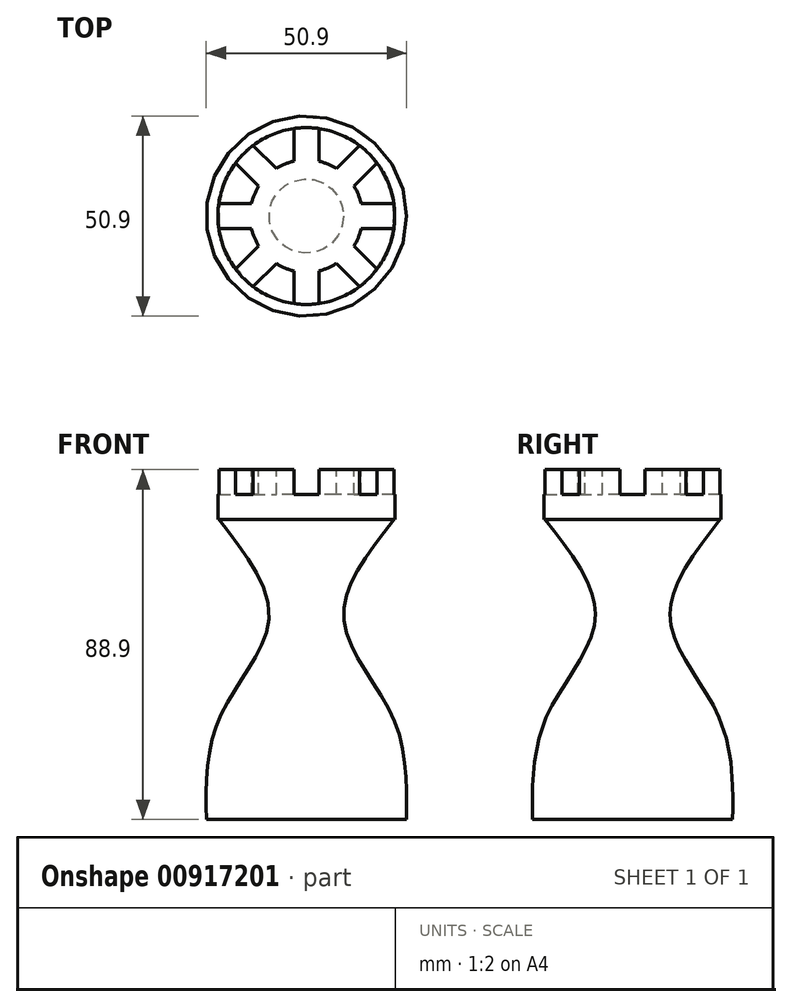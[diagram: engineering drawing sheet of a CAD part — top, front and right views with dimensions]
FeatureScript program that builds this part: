
annotation { "Feature Type Name" : "Feature", "Feature Type Description" : "" }
export const myFeature = defineFeature(function(context is Context, id is Id, definition is map)
    precondition{}
    {
        {
            var Q0;
            Q0=qCreatedBy(makeId("Top.planeOp"),FACE);
            var sketch = newSketch(context, id + "F0", { "sketchPlane" : qUnion([Q0])});
            skCircle(sketch, "E0", {"center": v(0, 0) * mm, "radius": 25.4 * mm});
            skSolve(sketch);
        }
        {
            var Q0;
            Q0=qCreatedBy(makeId("Top.planeOp"),FACE);
            cPlane(context, id + "F1", {"entities" : qUnion([Q0]), "cplaneType" : CPlaneType.OFFSET, "offset" : 25.4 * mm, "width" : 152.4 * mm, "height" : 152.4 * mm});
        }
        {
            var Q0;
            Q0=qCreatedBy(id+"F1.planeOp",FACE);
            var sketch = newSketch(context, id + "F2", { "sketchPlane" : qUnion([Q0])});
            skCircle(sketch, "E1", {"center": v(0, 0) * mm, "radius": 22.23 * mm});
            skSolve(sketch);
        }
        {
            var Q0;
            Q0=qCreatedBy(id+"F1.planeOp",FACE);
            cPlane(context, id + "F3", {"entities" : qUnion([Q0]), "cplaneType" : CPlaneType.OFFSET, "offset" : 25.4 * mm, "width" : 152.4 * mm, "height" : 152.4 * mm});
        }
        {
            var Q0;
            Q0=qCreatedBy(id+"F3.planeOp",FACE);
            var sketch = newSketch(context, id + "F4", { "sketchPlane" : qUnion([Q0])});
            skCircle(sketch, "E2", {"center": v(0, 0) * mm, "radius": 9.52 * mm});
            skSolve(sketch);
        }
        {
            var Q0;
            Q0=qCreatedBy(id+"F3.planeOp",FACE);
            cPlane(context, id + "F5", {"entities" : qUnion([Q0]), "cplaneType" : CPlaneType.OFFSET, "offset" : 25.4 * mm, "width" : 152.4 * mm, "height" : 152.4 * mm});
        }
        {
            var Q0;
            Q0=qCreatedBy(id+"F5.planeOp",FACE);
            var sketch = newSketch(context, id + "F6", { "sketchPlane" : qUnion([Q0])});
            skCircle(sketch, "E3", {"center": v(0, 0) * mm, "radius": 22.23 * mm});
            skSolve(sketch);
        }
        {
            var Q0;
            Q0 = qSketchRegion(id + "F0", true);
            var Q1;
            Q1 = qSketchRegion(id + "F2", true);
            var Q2;
            Q2 = qSketchRegion(id + "F4", true);
            var Q3;
            Q3 = qSketchRegion(id + "F6", true);
            loft(context, id + "F7", {"sheetProfilesArray" : [{ "sheetProfileEntities" : qUnion([Q0]) }, { "sheetProfileEntities" : qUnion([Q1]) }, { "sheetProfileEntities" : qUnion([Q2]) }, { "sheetProfileEntities" : qUnion([Q3]) }]});
        }
        {
            var Q0;
            Q0=makeQuery(id+"F7.opLoft","CAP_FACE",FACE,{"disambiguationData":[OSD([makeQuery(id+"F6.imprint","IMPRINT",FACE,{"disambiguationData":[TD([[makeQuery(id+"F6.imprint","IMPRINT",EDGE,{"derivedFrom":sQuery(id+"F6.wireOp",EDGE,"E3")}),1.0]])]})])],"isStart":true});
            var sketch = newSketch(context, id + "F8", { "sketchPlane" : qUnion([Q0])});
            skCircle(sketch, "E4", {"center": v(0, 0) * mm, "radius": 22.46 * mm});
            skFitSpline(sketch, "E5.0", {"points": [v(22.23, 0) * mm, v(22.23, 0.7) * mm, v(22.2, 1.42) * mm, v(22.12, 2.14) * mm, v(22.12, 2.18) * mm, v(22.05, 2.86) * mm, v(21.95, 3.58) * mm, v(21.8, 4.3) * mm, v(21.8, 4.34) * mm, v(21.66, 5.01) * mm, v(21.49, 5.72) * mm, v(21.28, 6.41) * mm, v(21.27, 6.45) * mm, v(21.07, 7.11) * mm, v(20.82, 7.8) * mm, v(20.55, 8.47) * mm, v(20.53, 8.5) * mm, v(20.27, 9.14) * mm, v(19.96, 9.8) * mm, v(19.62, 10.44) * mm, v(19.6, 10.48) * mm, v(19.28, 11.08) * mm, v(18.9, 11.7) * mm, v(18.5, 12.32) * mm, v(18.48, 12.35) * mm, v(18.1, 12.92) * mm, v(17.66, 13.5) * mm, v(17.2, 14.07) * mm, v(17.18, 14.1) * mm, v(16.74, 14.63) * mm, v(16.26, 15.17) * mm, v(15.74, 15.69) * mm, v(15.72, 15.72) * mm, v(15.23, 16.2) * mm, v(14.7, 16.7) * mm, v(14.13, 17.16) * mm, v(14.1, 17.18) * mm, v(13.57, 17.62) * mm, v(12.98, 18.05) * mm, v(12.38, 18.46) * mm, v(12.35, 18.48) * mm, v(11.77, 18.86) * mm, v(11.15, 19.24) * mm, v(10.51, 19.58) * mm, v(10.48, 19.6) * mm, v(9.87, 19.93) * mm, v(9.21, 20.24) * mm, v(8.54, 20.52) * mm, v(8.5, 20.53) * mm, v(7.87, 20.8) * mm, v(7.18, 21.04) * mm, v(6.49, 21.26) * mm, v(6.45, 21.27) * mm, v(5.8, 21.47) * mm, v(5.09, 21.65) * mm, v(4.37, 21.8) * mm, v(4.34, 21.8) * mm, v(3.66, 21.93) * mm, v(2.94, 22.04) * mm, v(2.22, 22.11) * mm, v(2.18, 22.12) * mm, v(1.5, 22.19) * mm, v(0.77, 22.22) * mm, v(0.04, 22.22) * mm, v(0, 22.23) * mm, v(-0.69, 22.23) * mm, v(-1.42, 22.2) * mm, v(-2.14, 22.12) * mm, v(-2.18, 22.12) * mm, v(-2.86, 22.05) * mm, v(-3.58, 21.95) * mm, v(-4.3, 21.8) * mm, v(-4.34, 21.8) * mm, v(-5.01, 21.66) * mm, v(-5.72, 21.49) * mm, v(-6.41, 21.28) * mm, v(-6.45, 21.27) * mm, v(-7.11, 21.07) * mm, v(-7.8, 20.82) * mm, v(-8.47, 20.55) * mm, v(-8.5, 20.53) * mm, v(-9.14, 20.27) * mm, v(-9.8, 19.96) * mm, v(-10.44, 19.62) * mm, v(-10.48, 19.6) * mm, v(-11.08, 19.28) * mm, v(-11.7, 18.9) * mm, v(-12.32, 18.5) * mm, v(-12.35, 18.48) * mm, v(-12.92, 18.1) * mm, v(-13.5, 17.66) * mm, v(-14.07, 17.2) * mm, v(-14.1, 17.18) * mm, v(-14.63, 16.74) * mm, v(-15.17, 16.26) * mm, v(-15.69, 15.74) * mm, v(-15.72, 15.72) * mm, v(-16.2, 15.23) * mm, v(-16.7, 14.7) * mm, v(-17.16, 14.13) * mm, v(-17.18, 14.1) * mm, v(-17.62, 13.57) * mm, v(-18.05, 12.98) * mm, v(-18.46, 12.38) * mm, v(-18.48, 12.35) * mm, v(-18.86, 11.77) * mm, v(-19.24, 11.15) * mm, v(-19.58, 10.51) * mm, v(-19.6, 10.48) * mm, v(-19.93, 9.87) * mm, v(-20.24, 9.21) * mm, v(-20.52, 8.54) * mm, v(-20.53, 8.5) * mm, v(-20.8, 7.87) * mm, v(-21.04, 7.18) * mm, v(-21.26, 6.49) * mm, v(-21.27, 6.45) * mm, v(-21.47, 5.8) * mm, v(-21.65, 5.09) * mm, v(-21.8, 4.37) * mm, v(-21.8, 4.34) * mm, v(-21.93, 3.66) * mm, v(-22.04, 2.94) * mm, v(-22.11, 2.22) * mm, v(-22.12, 2.18) * mm, v(-22.19, 1.5) * mm, v(-22.22, 0.77) * mm, v(-22.22, 0.04) * mm, v(-22.23, 0) * mm, v(-22.23, -0.69) * mm, v(-22.2, -1.42) * mm, v(-22.12, -2.14) * mm, v(-22.12, -2.18) * mm, v(-22.05, -2.86) * mm, v(-21.95, -3.58) * mm, v(-21.8, -4.3) * mm, v(-21.8, -4.34) * mm, v(-21.66, -5.01) * mm, v(-21.49, -5.72) * mm, v(-21.28, -6.41) * mm, v(-21.27, -6.45) * mm, v(-21.07, -7.11) * mm, v(-20.82, -7.8) * mm, v(-20.55, -8.47) * mm, v(-20.53, -8.5) * mm, v(-20.27, -9.14) * mm, v(-19.96, -9.8) * mm, v(-19.62, -10.44) * mm, v(-19.6, -10.48) * mm, v(-19.28, -11.08) * mm, v(-18.9, -11.7) * mm, v(-18.5, -12.32) * mm, v(-18.48, -12.35) * mm, v(-18.1, -12.92) * mm, v(-17.66, -13.5) * mm, v(-17.2, -14.07) * mm, v(-17.18, -14.1) * mm, v(-16.74, -14.63) * mm, v(-16.26, -15.17) * mm, v(-15.74, -15.69) * mm, v(-15.72, -15.72) * mm, v(-15.23, -16.2) * mm, v(-14.7, -16.7) * mm, v(-14.13, -17.16) * mm, v(-14.1, -17.18) * mm, v(-13.57, -17.62) * mm, v(-12.98, -18.05) * mm, v(-12.38, -18.46) * mm, v(-12.35, -18.48) * mm, v(-11.77, -18.86) * mm, v(-11.15, -19.24) * mm, v(-10.51, -19.58) * mm, v(-10.48, -19.6) * mm, v(-9.87, -19.93) * mm, v(-9.21, -20.24) * mm, v(-8.54, -20.52) * mm, v(-8.5, -20.53) * mm, v(-7.87, -20.8) * mm, v(-7.18, -21.04) * mm, v(-6.49, -21.26) * mm, v(-6.45, -21.27) * mm, v(-5.8, -21.47) * mm, v(-5.09, -21.65) * mm, v(-4.37, -21.8) * mm, v(-4.34, -21.8) * mm, v(-3.66, -21.93) * mm, v(-2.94, -22.04) * mm, v(-2.22, -22.11) * mm, v(-2.18, -22.12) * mm, v(-1.5, -22.19) * mm, v(-0.77, -22.22) * mm, v(-0.04, -22.22) * mm, v(0, -22.23) * mm, v(0.69, -22.23) * mm, v(1.42, -22.2) * mm, v(2.14, -22.12) * mm, v(2.18, -22.12) * mm, v(2.86, -22.05) * mm, v(3.58, -21.95) * mm, v(4.3, -21.8) * mm, v(4.34, -21.8) * mm, v(5.01, -21.66) * mm, v(5.72, -21.49) * mm, v(6.41, -21.28) * mm, v(6.45, -21.27) * mm, v(7.11, -21.07) * mm, v(7.8, -20.82) * mm, v(8.47, -20.55) * mm, v(8.5, -20.53) * mm, v(9.14, -20.27) * mm, v(9.8, -19.96) * mm, v(10.44, -19.62) * mm, v(10.48, -19.6) * mm, v(11.08, -19.28) * mm, v(11.7, -18.9) * mm, v(12.32, -18.5) * mm, v(12.35, -18.48) * mm, v(12.92, -18.1) * mm, v(13.5, -17.66) * mm, v(14.07, -17.2) * mm, v(14.1, -17.18) * mm, v(14.63, -16.74) * mm, v(15.17, -16.26) * mm, v(15.69, -15.74) * mm, v(15.72, -15.72) * mm, v(16.2, -15.23) * mm, v(16.7, -14.7) * mm, v(17.16, -14.13) * mm, v(17.18, -14.1) * mm, v(17.62, -13.57) * mm, v(18.05, -12.98) * mm, v(18.46, -12.38) * mm, v(18.48, -12.35) * mm, v(18.86, -11.77) * mm, v(19.24, -11.15) * mm, v(19.58, -10.51) * mm, v(19.6, -10.48) * mm, v(19.93, -9.87) * mm, v(20.24, -9.21) * mm, v(20.52, -8.54) * mm, v(20.53, -8.5) * mm, v(20.8, -7.87) * mm, v(21.04, -7.18) * mm, v(21.26, -6.49) * mm, v(21.27, -6.45) * mm, v(21.47, -5.8) * mm, v(21.65, -5.09) * mm, v(21.8, -4.37) * mm, v(21.8, -4.34) * mm, v(21.93, -3.66) * mm, v(22.04, -2.94) * mm, v(22.11, -2.22) * mm, v(22.12, -2.18) * mm, v(22.19, -1.45) * mm, v(22.23, -0.73) * mm, v(22.23, 0) * mm, v(22.23, 0) * mm]});
            skSolve(sketch);
        }
        {
            var Q0;
            Q0 = qSketchRegion(id + "F8", true);
            var Q1;
            Q1=makeQuery(id+"F8.imprint","IMPRINT",FACE,{"disambiguationData":[TD([[makeQuery(id+"F8.imprint","IMPRINT",EDGE,{"derivedFrom":sQuery(id+"F8.wireOp",EDGE,"E5.0")}),1.0]])]});
            extrude(context, id + "F9", {"entities" : qUnion([Q0, Q1]), "depth" : 12.7 * mm, "offsetDistance" : 25.4 * mm});
        }
        {
            var Q0;
            Q0=makeQuery(id+"F9.opExtrude","CAP_FACE",FACE,{"disambiguationData":[OSD([sQuery(id+"F8.wireOp",EDGE,"E4")])],"isStart":false});
            var sketch = newSketch(context, id + "F10", { "sketchPlane" : qUnion([Q0])});
            skLineSegment(sketch, "E6", {"start": v(0, 0) * mm, "end": v(19.57, 0) * mm, "construction": true});
            skCircle(sketch, "E7", {"center": v(0, 0) * mm, "radius": 14.29 * mm});
            skLineSegment(sketch, "E8.bottom", {"start": v(27.54, -3.17) * mm, "end": v(11.6, -3.17) * mm});
            skLineSegment(sketch, "E8.top", {"start": v(27.54, 3.18) * mm, "end": v(11.6, 3.18) * mm});
            skLineSegment(sketch, "E8.left", {"start": v(27.54, -3.17) * mm, "end": v(27.54, 3.18) * mm});
            skLineSegment(sketch, "E8.right", {"start": v(11.6, -3.17) * mm, "end": v(11.6, 3.18) * mm});
            skPoint(sketch, "E8.middle", {"position": v(19.57, 0) * mm});
            skLineSegment(sketch, "E9.1.0", {"start": v(17.23, 21.72) * mm, "end": v(5.96, 10.45) * mm});
            skLineSegment(sketch, "E9.1.1", {"start": v(21.72, 17.23) * mm, "end": v(10.45, 5.96) * mm});
            skLineSegment(sketch, "E9.1.2", {"start": v(21.72, 17.23) * mm, "end": v(17.23, 21.72) * mm});
            skPoint(sketch, "E9.1.3", {"position": v(13.84, 13.84) * mm});
            skLineSegment(sketch, "E9.1.4", {"start": v(10.45, 5.96) * mm, "end": v(5.96, 10.45) * mm});
            skLineSegment(sketch, "E9.2.0", {"start": v(-3.18, 27.54) * mm, "end": v(-3.18, 11.6) * mm});
            skLineSegment(sketch, "E9.2.1", {"start": v(3.17, 27.54) * mm, "end": v(3.18, 11.6) * mm});
            skLineSegment(sketch, "E9.2.2", {"start": v(3.17, 27.54) * mm, "end": v(-3.18, 27.54) * mm});
            skPoint(sketch, "E9.2.3", {"position": v(0, 19.57) * mm});
            skLineSegment(sketch, "E9.2.4", {"start": v(3.18, 11.6) * mm, "end": v(-3.18, 11.6) * mm});
            skLineSegment(sketch, "E9.3.0", {"start": v(-21.72, 17.23) * mm, "end": v(-10.45, 5.96) * mm});
            skLineSegment(sketch, "E9.3.1", {"start": v(-17.23, 21.72) * mm, "end": v(-5.96, 10.45) * mm});
            skLineSegment(sketch, "E9.3.2", {"start": v(-17.23, 21.72) * mm, "end": v(-21.72, 17.23) * mm});
            skPoint(sketch, "E9.3.3", {"position": v(-13.84, 13.84) * mm});
            skLineSegment(sketch, "E9.3.4", {"start": v(-5.96, 10.45) * mm, "end": v(-10.45, 5.96) * mm});
            skLineSegment(sketch, "E9.4.0", {"start": v(-27.54, -3.17) * mm, "end": v(-11.6, -3.18) * mm});
            skLineSegment(sketch, "E9.4.1", {"start": v(-27.54, 3.17) * mm, "end": v(-11.6, 3.18) * mm});
            skLineSegment(sketch, "E9.4.2", {"start": v(-27.54, 3.17) * mm, "end": v(-27.54, -3.18) * mm});
            skPoint(sketch, "E9.4.3", {"position": v(-19.57, 0) * mm});
            skLineSegment(sketch, "E9.4.4", {"start": v(-11.6, 3.18) * mm, "end": v(-11.6, -3.18) * mm});
            skLineSegment(sketch, "E9.5.0", {"start": v(-17.23, -21.72) * mm, "end": v(-5.96, -10.45) * mm});
            skLineSegment(sketch, "E9.5.1", {"start": v(-21.72, -17.23) * mm, "end": v(-10.45, -5.96) * mm});
            skLineSegment(sketch, "E9.5.2", {"start": v(-21.72, -17.23) * mm, "end": v(-17.23, -21.72) * mm});
            skPoint(sketch, "E9.5.3", {"position": v(-13.84, -13.84) * mm});
            skLineSegment(sketch, "E9.5.4", {"start": v(-10.45, -5.96) * mm, "end": v(-5.96, -10.45) * mm});
            skLineSegment(sketch, "E9.6.0", {"start": v(3.17, -27.54) * mm, "end": v(3.18, -11.6) * mm});
            skLineSegment(sketch, "E9.6.1", {"start": v(-3.18, -27.54) * mm, "end": v(-3.18, -11.6) * mm});
            skLineSegment(sketch, "E9.6.2", {"start": v(-3.18, -27.54) * mm, "end": v(3.17, -27.54) * mm});
            skPoint(sketch, "E9.6.3", {"position": v(0, -19.57) * mm});
            skLineSegment(sketch, "E9.6.4", {"start": v(-3.18, -11.6) * mm, "end": v(3.17, -11.6) * mm});
            skLineSegment(sketch, "E9.7.0", {"start": v(21.72, -17.23) * mm, "end": v(10.45, -5.96) * mm});
            skLineSegment(sketch, "E9.7.1", {"start": v(17.23, -21.72) * mm, "end": v(5.96, -10.45) * mm});
            skLineSegment(sketch, "E9.7.2", {"start": v(17.23, -21.72) * mm, "end": v(21.72, -17.23) * mm});
            skPoint(sketch, "E9.7.3", {"position": v(13.84, -13.84) * mm});
            skLineSegment(sketch, "E9.7.4", {"start": v(5.96, -10.45) * mm, "end": v(10.45, -5.96) * mm});
            skSolve(sketch);
        }
        {
            var Q0;
            Q0 = qSketchRegion(id + "F10", true);
            extrude(context, id + "F11", {"entities" : qUnion([Q0]), "operationType" : NewBodyOperationType.REMOVE, "oppositeDirection" : true, "depth" : 6.35 * mm, "offsetDistance" : 25.4 * mm});
        }
    });
